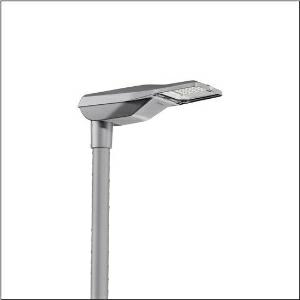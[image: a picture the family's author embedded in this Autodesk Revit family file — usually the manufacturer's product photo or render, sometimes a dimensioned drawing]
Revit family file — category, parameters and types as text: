
# Revit family: streetlight_sl_21_iq_micro___stw1_0a_5xe1e61d08cb_4749
name_source: partatom
category: Lighting Fixtures
units: mm (PartAtom-declared; Revit-internal decimal feet)

## family parameters
Cut with Voids When Loaded = No
Host = Face
Light Source = No
Part Type = Normal
Room Calculation Point = No
Round Connector Dimension = Use Diameter
Shared = No

## types (1)
- --- (1 x LED, 2570 lm, 19.4 W, 2700K)
    Apparent Load = 19 VA
    CIE Flux Codes = 38 75 98 100 100
    Color Rendering = 70
    Color Temperature = 2700K
    Default Elevation = 1800 mm
    Description = Streetlight SL 21 iQ micro, mast luminaire, primary light control with lens, of PMMA, primary optical cover: cover, of toughened safety glass, transparent, light distribution: STW1.0a, light emission: direct distribution, primary light characteristic: asymmetric, installation type: post-top, side-entry, LED, High Power LED, rated luminous flux: 2.570lm, luminous efficacy: 133lm/W, light colour: 727, colour temperature: 2700K, control gear: iQ-Comfort, control: Auto-Match, Temp-Guard, Lumen-Switch, Night-Set, Smart-Wire, Light-Fading, Desk-Remote (wireless, voltage-free reading and setting of iQ features in the workshop via application-optimized NFC function/RFID function), optimised constant luminous flux control (CLO 2.0), pre-setting: linear dimming characteristic, mains connection: 220..240V, AC, 50/60Hz, start of lifetime: 19W, end of service life: 20W, reduction: 10W, luminaire housing, of diecast aluminium, powder-coated, SITECO metallic grey (DB 702S), corrosivity category C5 high according to DIN EN ISO 12944, please order mast flange separately, inclination adjustable: 0°, 5°, 10°, 15°, sealing non-destructively replaceable, multi-level sealing system, length: 528mm, width: 235mm, height: 110mm, mast flange for spigot size: 42mm (side-entry): 5XC10008XM4, 60/48mm (side-entry/post-top): 5XC10108XM2, 76/60mm (side-entry/post-top): 5XC10108XM1, protection rating (complete): IP66, insulation class (complete): insulation class II (safety insulation), certification: CE, ENEC, ENEC+, VDE, impact resistance: IK10, permissible operating ambient temperature for outdoor applications: -40..+50°C, standard-compliant lighting for roads and squares, packaging unit: 1 piece

Light Distribution: STW1.0a
    Height = 110 mm
    Lamp = 1 x LED
    Lamp Light Flux = 2570 lm
    Lamp Power = 19.4 W
    Lamp count = 1
    Length = 528 mm
    Luminous efficacy = 132 lm/W
    Manufacturer = Siteco
    ModVariant = No
    Model = 5XE1E61D08CB
    Number of Poles = 1
    OnlyDefault = Yes
    Power Factor = 1
    Product Name = Streetlight SL 21 iQ micro | STW1.0a
    Product group = mast luminaire | pylon top
    ProductGroupID = 6100
    Protection Class = Protection class II
    Protection Degree = IP 66
    RLX_Detail_Level = 1
    RLX_Emergency_Light_Flux = 0 lm
    RLX_Emergency_Type = 0
    RLX_Emergency_Type_DB = No
    RlxData = <blob elided: 98725 chars, md5=ac40994e>
    Socket = socket
    Standby Power = 0 W
    System Light Flux = 2570 lm
    System Power = 19 W
    Type Comments = factory setting: luminous flux: 100 % | dim-lin: 254 | 387 mA
    Type Image = l_1006881.jpg
    URL = http://relux.com
    VarID = @adj_138247
    Voltage = 0 V
    Weight = 0.00 kg
    Width = 235 mm

## geometry (parser evidence)
native form markers: Blend x4, Sweep x11
no freeform markers — native parametric forms only
